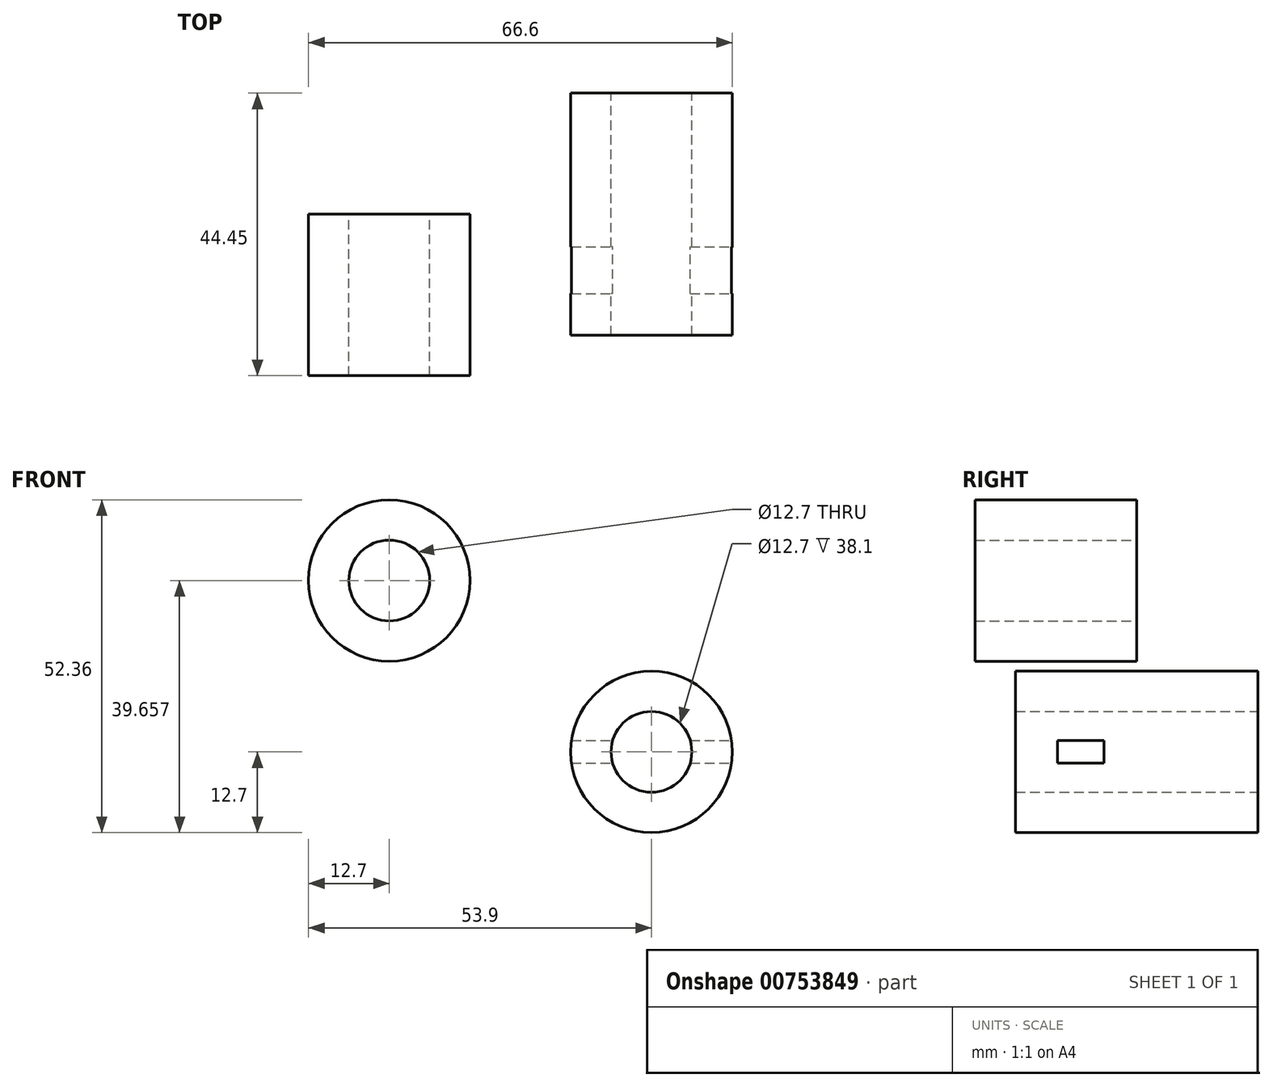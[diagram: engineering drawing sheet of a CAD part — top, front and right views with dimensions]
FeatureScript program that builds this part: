
annotation { "Feature Type Name" : "Feature", "Feature Type Description" : "" }
export const myFeature = defineFeature(function(context is Context, id is Id, definition is map)
    precondition{}
    {
        {
            var Q0;
            Q0=qCreatedBy(makeId("Front.planeOp"),FACE);
            var sketch = newSketch(context, id + "F0", { "sketchPlane" : qUnion([Q0])});
            skCircle(sketch, "E0", {"center": v(0, 0) * mm, "radius": 12.7 * mm});
            skCircle(sketch, "E1", {"center": v(0, 0) * mm, "radius": 6.35 * mm});
            skSolve(sketch);
        }
        {
            var Q0;
            Q0=makeQuery(id+"F0.imprint","IMPRINT",FACE,{"disambiguationData":[TD([[makeQuery(id+"F0.imprint","IMPRINT",EDGE,{"derivedFrom":sQuery(id+"F0.wireOp",EDGE,"E0")}),1.0]])]});
            var Q1;
            Q1=sQuery(id+"F0.wireOp",EDGE,"E0");
            extrude(context, id + "F1", {"entities" : qUnion([Q0]), "surfaceEntities" : qUnion([Q1]), "endBound" : BoundingType.SYMMETRIC, "depth" : 38.1 * mm, "offsetDistance" : 25.4 * mm});
        }
        {
            var Q0;
            Q0=qCreatedBy(makeId("Front.planeOp"),FACE);
            var sketch = newSketch(context, id + "F2", { "sketchPlane" : qUnion([Q0])});
            skCircle(sketch, "E2", {"center": v(-41.2, 26.96) * mm, "radius": 12.7 * mm});
            skCircle(sketch, "E3", {"center": v(-41.2, 26.96) * mm, "radius": 6.35 * mm});
            skSolve(sketch);
        }
        {
            var Q0;
            Q0=makeQuery(id+"F2.imprint","IMPRINT",FACE,{"disambiguationData":[TD([[makeQuery(id+"F2.imprint","IMPRINT",EDGE,{"derivedFrom":sQuery(id+"F2.wireOp",EDGE,"E2")}),1.0]])]});
            extrude(context, id + "F3", {"entities" : qUnion([Q0]), "depth" : 25.4 * mm, "offsetDistance" : 25.4 * mm});
        }
        {
            var Q0;
            Q0=qCreatedBy(makeId("Right.planeOp"),FACE);
            var sketch = newSketch(context, id + "F4", { "sketchPlane" : qUnion([Q0])});
            skLineSegment(sketch, "E4.bottom", {"start": v(-5.14, -1.78) * mm, "end": v(-12.45, -1.78) * mm});
            skLineSegment(sketch, "E4.top", {"start": v(-5.14, 1.78) * mm, "end": v(-12.45, 1.78) * mm});
            skLineSegment(sketch, "E4.left", {"start": v(-5.14, -1.78) * mm, "end": v(-5.14, 1.78) * mm});
            skLineSegment(sketch, "E4.right", {"start": v(-12.45, -1.78) * mm, "end": v(-12.45, 1.78) * mm});
            skSolve(sketch);
        }
        {
            var Q0;
            Q0=makeQuery(id+"F4.imprint","IMPRINT",FACE,{"disambiguationData":[TD([[makeQuery(id+"F4.imprint","IMPRINT",EDGE,{"derivedFrom":sQuery(id+"F4.wireOp",EDGE,"E4.bottom")}),-1.0]])]});
            extrude(context, id + "F5", {"entities" : qUnion([Q0]), "operationType" : NewBodyOperationType.REMOVE, "endBound" : BoundingType.SYMMETRIC, "oppositeDirection" : true, "depth" : 25.4 * mm, "offsetDistance" : 25.4 * mm});
        }
    });
